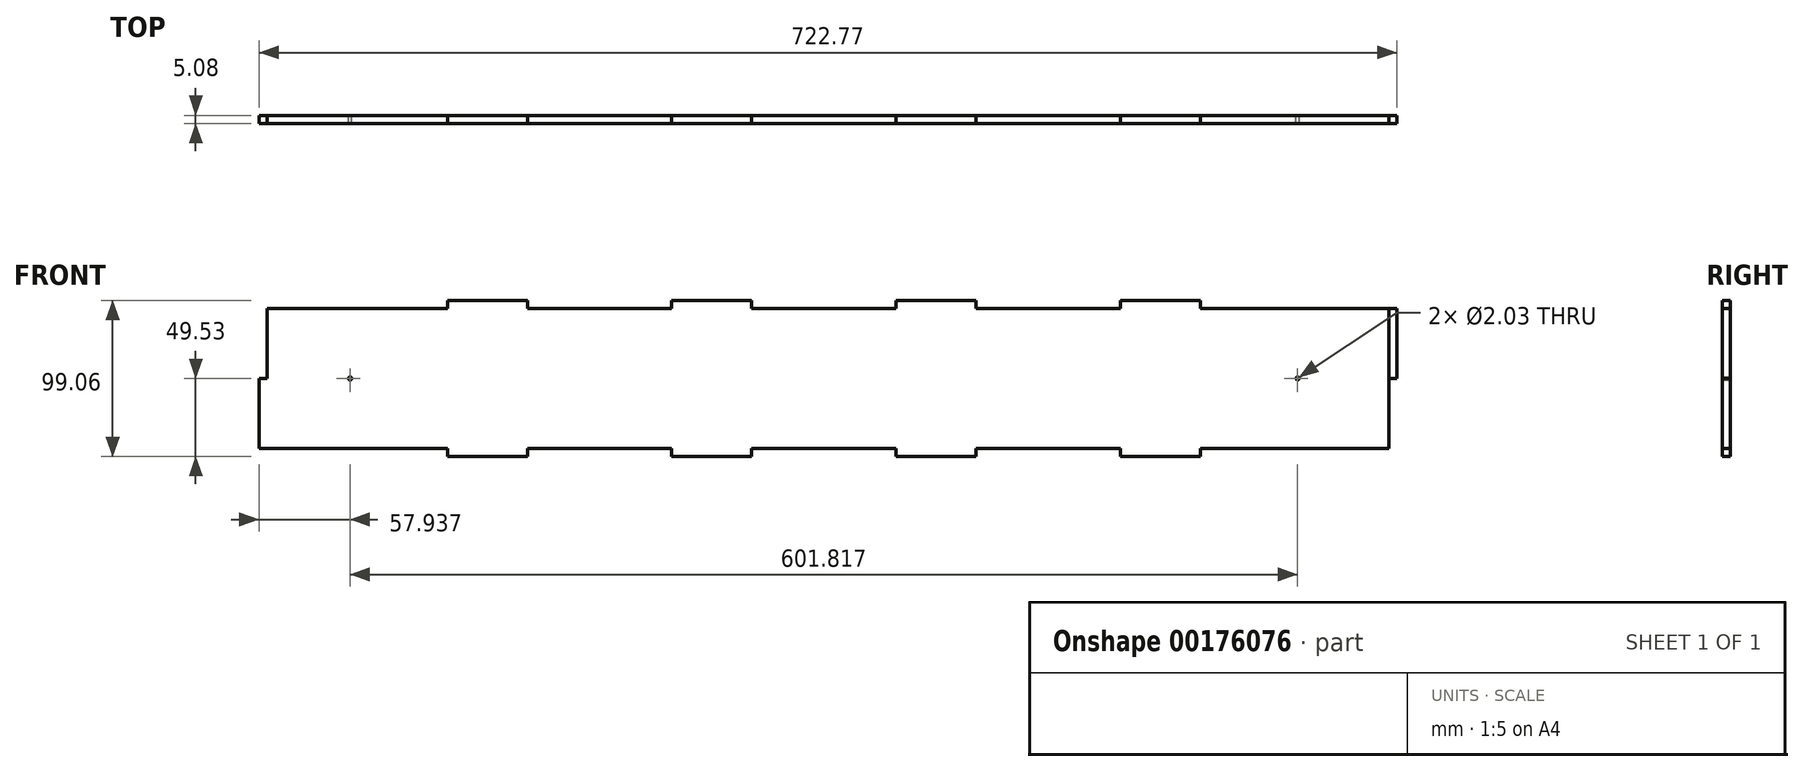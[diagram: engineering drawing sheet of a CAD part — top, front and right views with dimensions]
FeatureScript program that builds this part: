
annotation { "Feature Type Name" : "Feature", "Feature Type Description" : "" }
export const myFeature = defineFeature(function(context is Context, id is Id, definition is map)
    precondition{}
    {
        {
            var Q0;
            Q0=qCreatedBy(makeId("Front.planeOp"),FACE);
            var sketch = newSketch(context, id + "F0", { "sketchPlane" : qUnion([Q0])});
            skLineSegment(sketch, "E0.bottom", {"start": v(0, 0) * mm, "end": v(717.7, 0) * mm});
            skLineSegment(sketch, "E0.top", {"start": v(0, 88.9) * mm, "end": v(717.7, 88.9) * mm});
            skLineSegment(sketch, "E0.left", {"start": v(0, 0) * mm, "end": v(0, 88.9) * mm});
            skLineSegment(sketch, "E0.right", {"start": v(717.7, 0) * mm, "end": v(717.7, 88.9) * mm});
            skLineSegment(sketch, "E1", {"start": v(0, 44.45) * mm, "end": v(717.7, 44.45) * mm, "construction": true});
            skLineSegment(sketch, "E2", {"start": v(203.1, 88.9) * mm, "end": v(203.1, 0) * mm, "construction": true});
            skLineSegment(sketch, "E3", {"start": v(229.7, 0) * mm, "end": v(229.7, 88.9) * mm, "construction": true});
            skLineSegment(sketch, "E4", {"start": v(345.55, 88.9) * mm, "end": v(345.55, 0) * mm, "construction": true});
            skLineSegment(sketch, "E5", {"start": v(372.14, 0) * mm, "end": v(372.14, 88.9) * mm, "construction": true});
            skLineSegment(sketch, "E6", {"start": v(488, 0) * mm, "end": v(488, 88.9) * mm, "construction": true});
            skLineSegment(sketch, "E7", {"start": v(514.6, 88.9) * mm, "end": v(514.6, 0) * mm, "construction": true});
            skLineSegment(sketch, "E8", {"start": v(119.79, 88.9) * mm, "end": v(119.79, 93.98) * mm});
            skLineSegment(sketch, "E9", {"start": v(119.79, 93.98) * mm, "end": v(170.59, 93.98) * mm});
            skLineSegment(sketch, "E10", {"start": v(170.59, 93.98) * mm, "end": v(170.59, 88.9) * mm});
            skLineSegment(sketch, "E11", {"start": v(262.22, 88.9) * mm, "end": v(262.22, 93.98) * mm});
            skLineSegment(sketch, "E12", {"start": v(262.22, 93.98) * mm, "end": v(313.02, 93.98) * mm});
            skLineSegment(sketch, "E13", {"start": v(313.02, 93.98) * mm, "end": v(313.02, 88.9) * mm});
            skLineSegment(sketch, "E14", {"start": v(404.67, 88.9) * mm, "end": v(404.67, 93.98) * mm});
            skLineSegment(sketch, "E15", {"start": v(404.67, 93.98) * mm, "end": v(455.47, 93.98) * mm});
            skLineSegment(sketch, "E16", {"start": v(455.47, 93.98) * mm, "end": v(455.47, 88.9) * mm});
            skLineSegment(sketch, "E17", {"start": v(455.47, 88.9) * mm, "end": v(547.1, 88.9) * mm});
            skLineSegment(sketch, "E18", {"start": v(547.1, 88.9) * mm, "end": v(547.1, 93.98) * mm});
            skLineSegment(sketch, "E19", {"start": v(547.1, 93.98) * mm, "end": v(597.9, 93.98) * mm});
            skLineSegment(sketch, "E20", {"start": v(597.9, 93.98) * mm, "end": v(597.9, 88.9) * mm});
            skLineSegment(sketch, "E21", {"start": v(229.7, 62.66) * mm, "end": v(345.55, 62.66) * mm, "construction": true});
            skLineSegment(sketch, "E22", {"start": v(372.14, 62.9) * mm, "end": v(488, 62.9) * mm, "construction": true});
            skPoint(sketch, "E23", {"position": v(287.62, 62.66) * mm});
            skPoint(sketch, "E24", {"position": v(430.07, 62.9) * mm});
            skPoint(sketch, "E25", {"position": v(287.62, 93.98) * mm});
            skPoint(sketch, "E26", {"position": v(430.07, 93.98) * mm});
            skLineSegment(sketch, "E27.MirrorCS", {"start": v(597.9, -5.08) * mm, "end": v(597.9, 0) * mm});
            skLineSegment(sketch, "E28.MirrorCS", {"start": v(547.1, -5.08) * mm, "end": v(597.9, -5.08) * mm});
            skLineSegment(sketch, "E29.MirrorCS", {"start": v(547.1, 0) * mm, "end": v(547.1, -5.08) * mm});
            skLineSegment(sketch, "E30.MirrorCS", {"start": v(455.47, -5.08) * mm, "end": v(455.47, 0) * mm});
            skLineSegment(sketch, "E31.MirrorCS", {"start": v(404.67, -5.08) * mm, "end": v(455.47, -5.08) * mm});
            skLineSegment(sketch, "E32.MirrorCS", {"start": v(404.67, 0) * mm, "end": v(404.67, -5.08) * mm});
            skLineSegment(sketch, "E33.MirrorCS", {"start": v(313.02, -5.08) * mm, "end": v(313.02, 0) * mm});
            skLineSegment(sketch, "E34.MirrorCS", {"start": v(262.22, -5.08) * mm, "end": v(313.02, -5.08) * mm});
            skLineSegment(sketch, "E35.MirrorCS", {"start": v(262.22, 0) * mm, "end": v(262.22, -5.08) * mm});
            skLineSegment(sketch, "E36.MirrorCS", {"start": v(170.59, -5.08) * mm, "end": v(170.59, 0) * mm});
            skLineSegment(sketch, "E37.MirrorCS", {"start": v(119.79, 0) * mm, "end": v(119.79, -5.08) * mm});
            skLineSegment(sketch, "E38.MirrorCS", {"start": v(119.79, -5.08) * mm, "end": v(170.59, -5.08) * mm});
            skCircle(sketch, "E39", {"center": v(57.94, 44.45) * mm, "radius": 1.02 * mm});
            skCircle(sketch, "E40", {"center": v(659.75, 44.45) * mm, "radius": 1.02 * mm});
            skLineSegment(sketch, "E41", {"start": v(358.85, 88.9) * mm, "end": v(358.85, 0) * mm, "construction": true});
            skSolve(sketch);
        }
        {
            var Q0;
            {var subQ3=sQuery(id+"F0.wireOp",EDGE,"E0.left");Q0=makeQuery(id+"F0.imprint","IMPRINT",FACE,{"disambiguationData":[TD([[makeQuery(id+"F0.imprint","IMPRINT",EDGE,{"derivedFrom":subQ3}),-1.0]])]});}
            var Q1;
            {var subQ0=sQuery(id+"F0.wireOp",EDGE,"E8");Q1=makeQuery(id+"F0.imprint","IMPRINT",FACE,{"disambiguationData":[TD([[makeQuery(id+"F0.imprint","IMPRINT",EDGE,{"derivedFrom":subQ0}),-1.0]])]});}
            var Q2;
            {var subQ0=sQuery(id+"F0.wireOp",EDGE,"E36.MirrorCS");Q2=makeQuery(id+"F0.imprint","IMPRINT",FACE,{"disambiguationData":[TD([[makeQuery(id+"F0.imprint","IMPRINT",EDGE,{"derivedFrom":subQ0}),1.0]])]});}
            var Q3;
            {var subQ0=sQuery(id+"F0.wireOp",EDGE,"E33.MirrorCS");Q3=makeQuery(id+"F0.imprint","IMPRINT",FACE,{"disambiguationData":[TD([[makeQuery(id+"F0.imprint","IMPRINT",EDGE,{"derivedFrom":subQ0}),1.0]])]});}
            var Q4;
            {var subQ0=sQuery(id+"F0.wireOp",EDGE,"E11");Q4=makeQuery(id+"F0.imprint","IMPRINT",FACE,{"disambiguationData":[TD([[makeQuery(id+"F0.imprint","IMPRINT",EDGE,{"derivedFrom":subQ0}),-1.0]])]});}
            var Q5;
            {var subQ0=sQuery(id+"F0.wireOp",EDGE,"E14");Q5=makeQuery(id+"F0.imprint","IMPRINT",FACE,{"disambiguationData":[TD([[makeQuery(id+"F0.imprint","IMPRINT",EDGE,{"derivedFrom":subQ0}),-1.0]])]});}
            var Q6;
            {var subQ0=sQuery(id+"F0.wireOp",EDGE,"E30.MirrorCS");Q6=makeQuery(id+"F0.imprint","IMPRINT",FACE,{"disambiguationData":[TD([[makeQuery(id+"F0.imprint","IMPRINT",EDGE,{"derivedFrom":subQ0}),1.0]])]});}
            var Q7;
            {var subQ0=sQuery(id+"F0.wireOp",EDGE,"E18");Q7=makeQuery(id+"F0.imprint","IMPRINT",FACE,{"disambiguationData":[TD([[makeQuery(id+"F0.imprint","IMPRINT",EDGE,{"derivedFrom":subQ0}),-1.0]])]});}
            var Q8;
            {var subQ0=sQuery(id+"F0.wireOp",EDGE,"E27.MirrorCS");Q8=makeQuery(id+"F0.imprint","IMPRINT",FACE,{"disambiguationData":[TD([[makeQuery(id+"F0.imprint","IMPRINT",EDGE,{"derivedFrom":subQ0}),1.0]])]});}
            extrude(context, id + "F1", {"entities" : qUnion([Q0, Q1, Q2, Q3, Q4, Q5, Q6, Q7, Q8]), "depth" : 5.08 * mm});
        }
        {
            var Q0;
            Q0=makeQuery(id+"F1.opExtrude","CAP_FACE",FACE,{"disambiguationData":[OSD([sQuery(id+"F0.wireOp",EDGE,"E0.bottom"),sQuery(id+"F0.wireOp",EDGE,"E0.top"),sQuery(id+"F0.wireOp",EDGE,"E0.left"),sQuery(id+"F0.wireOp",EDGE,"E0.right"),sQuery(id+"F0.wireOp",EDGE,"E8"),sQuery(id+"F0.wireOp",EDGE,"E9"),sQuery(id+"F0.wireOp",EDGE,"E10"),sQuery(id+"F0.wireOp",EDGE,"E11"),sQuery(id+"F0.wireOp",EDGE,"E12"),sQuery(id+"F0.wireOp",EDGE,"E13"),sQuery(id+"F0.wireOp",EDGE,"E14"),sQuery(id+"F0.wireOp",EDGE,"E15"),sQuery(id+"F0.wireOp",EDGE,"E16"),sQuery(id+"F0.wireOp",EDGE,"E17"),sQuery(id+"F0.wireOp",EDGE,"E18"),sQuery(id+"F0.wireOp",EDGE,"E19"),sQuery(id+"F0.wireOp",EDGE,"E20"),sQuery(id+"F0.wireOp",EDGE,"E27.MirrorCS"),sQuery(id+"F0.wireOp",EDGE,"E28.MirrorCS"),sQuery(id+"F0.wireOp",EDGE,"E29.MirrorCS"),sQuery(id+"F0.wireOp",EDGE,"E30.MirrorCS"),sQuery(id+"F0.wireOp",EDGE,"E31.MirrorCS"),sQuery(id+"F0.wireOp",EDGE,"E32.MirrorCS"),sQuery(id+"F0.wireOp",EDGE,"E33.MirrorCS"),sQuery(id+"F0.wireOp",EDGE,"E34.MirrorCS"),sQuery(id+"F0.wireOp",EDGE,"E35.MirrorCS"),sQuery(id+"F0.wireOp",EDGE,"E36.MirrorCS"),sQuery(id+"F0.wireOp",EDGE,"E37.MirrorCS"),sQuery(id+"F0.wireOp",EDGE,"E38.MirrorCS"),sQuery(id+"F0.wireOp",EDGE,"E39"),sQuery(id+"F0.wireOp",EDGE,"E40")])],"isStart":false});
            var sketch = newSketch(context, id + "F2", { "sketchPlane" : qUnion([Q0])});
            skLineSegment(sketch, "E42.bottom", {"start": v(0, 44.45) * mm, "end": v(5.08, 44.45) * mm});
            skLineSegment(sketch, "E42.top", {"start": v(0, 88.9) * mm, "end": v(5.08, 88.9) * mm});
            skLineSegment(sketch, "E42.left", {"start": v(0, 44.45) * mm, "end": v(0, 88.9) * mm});
            skLineSegment(sketch, "E42.right", {"start": v(5.08, 44.45) * mm, "end": v(5.08, 88.9) * mm});
            skPoint(sketch, "E43", {"position": v(5.08, 66.67) * mm});
            skPoint(sketch, "E44", {"position": v(57.94, 44.45) * mm});
            skLineSegment(sketch, "E45.bottom", {"start": v(717.7, 44.45) * mm, "end": v(722.77, 44.45) * mm});
            skLineSegment(sketch, "E45.top", {"start": v(717.7, 88.9) * mm, "end": v(722.77, 88.9) * mm});
            skLineSegment(sketch, "E45.right", {"start": v(722.77, 44.45) * mm, "end": v(722.77, 88.9) * mm});
            skPoint(sketch, "E46", {"position": v(722.77, 66.68) * mm});
            skPoint(sketch, "E47", {"position": v(659.75, 44.45) * mm});
            skSolve(sketch);
        }
        {
            var Q0;
            Q0=makeQuery(id+"F2.imprint","IMPRINT",FACE,{"disambiguationData":[TD([[makeQuery(id+"F2.imprint","IMPRINT",EDGE,{"derivedFrom":sQuery(id+"F2.wireOp",EDGE,"E42.bottom")}),1.0]])]});
            extrude(context, id + "F3", {"entities" : qUnion([Q0]), "operationType" : NewBodyOperationType.REMOVE, "endBound" : BoundingType.THROUGH_ALL, "oppositeDirection" : true, "depth" : 25.4 * mm});
        }
        {
            var Q0;
            Q0=makeQuery(id+"F2.imprint","IMPRINT",FACE,{"disambiguationData":[TD([[makeQuery(id+"F2.imprint","IMPRINT",EDGE,{"derivedFrom":sQuery(id+"F2.wireOp",EDGE,"E45.bottom")}),1.0]])]});
            extrude(context, id + "F4", {"entities" : qUnion([Q0]), "oppositeDirection" : true, "depth" : 5.08 * mm});
        }
    });
